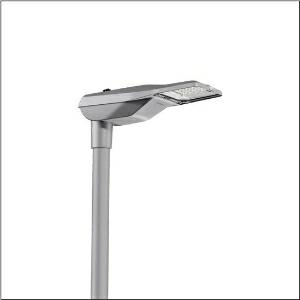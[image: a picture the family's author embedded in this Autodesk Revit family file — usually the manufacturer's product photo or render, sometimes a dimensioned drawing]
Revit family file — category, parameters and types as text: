
# Revit family: streetlight_sl_21_iq_micro___p0_8a_5xe1u31v08cb_453e
name_source: partatom
category: Lighting Fixtures
units: mm (PartAtom-declared; Revit-internal decimal feet)

## family parameters
Cut with Voids When Loaded = No
Host = Face
Light Source = No
Part Type = Normal
Room Calculation Point = No
Round Connector Dimension = Use Diameter
Shared = No

## types (1)
- --- (1 x LED, 2890 lm, 19.1 W, 3000K)
    Apparent Load = 19 VA
    CIE Flux Codes = 33 69 96 100 100
    Color Rendering = 70
    Color Temperature = 3000K
    Default Elevation = 1800 mm
    Description = Streetlight SL 21 iQ micro, mast luminaire, primary light control with lens, of PMMA, primary optical cover: cover, of toughened safety glass, transparent, light distribution: P0.8a, light emission: direct distribution, primary light characteristic: asymmetric, installation type: post-top, side-entry, LED, High Power LED, rated luminous flux: 2.890lm, luminous efficacy: 151lm/W, light colour: 730, colour temperature: 3000K, control gear: iQ-Street Remote, D4i with power reduction, control: pre-setting: logarithmic dimming characteristic, Street-Remote, Auto-Match, Temp-Guard, Lumen-Switch, Night-Set, Smart-Wire, Light-Fading, Desk-Remote (wireless, voltage-free reading and setting of iQ features in the workshop via application-optimized NFC function/RFID function), optimised constant luminous flux control (CLO 2.0), mains connection: 220..240V, AC, 50/60Hz, start of lifetime: 19W, end of service life: 20W, reduction: 9W, luminaire housing, of diecast aluminium, powder-coated, SITECO metallic grey (DB 702S), corrosivity category C5 high according to DIN EN ISO 12944, please order mast flange separately, inclination adjustable: 0°, 5°, 10°, 15°, sealing non-destructively replaceable, multi-level sealing system, length: 528mm, width: 235mm, height: 110mm, mast flange for spigot size: 42mm (side-entry): 5XC10008XM4, 60/48mm (side-entry/post-top): 5XC10108XM2, 76/60mm (side-entry/post-top): 5XC10108XM1, mounting height: 4..8m, Smart Interface above, protection rating (complete): IP66, insulation class (complete): insulation class II (safety insulation), certification: CE, ENEC, ENEC+, VDE, impact resistance: IK10, permissible operating ambient temperature for outdoor applications: -40..+50°C, standard-compliant lighting for roads and squares, packaging unit: 1 piece

Light Distribution: P0.8a
    Height = 110 mm
    Lamp = 1 x LED
    Lamp Light Flux = 2890 lm
    Lamp Power = 19.1 W
    Lamp count = 1
    Length = 528 mm
    Luminous efficacy = 151 lm/W
    Manufacturer = Siteco
    ModVariant = No
    Model = 5XE1U31V08CB
    Number of Poles = 1
    OnlyDefault = Yes
    Power Factor = 1
    Product Name = Streetlight SL 21 iQ micro | P0.8a
    Product group = mast luminaire | pylon top
    ProductGroupID = 6100
    Protection Class = Protection class II
    Protection Degree = IP 66
    RLX_Detail_Level = 1
    RLX_Emergency_Light_Flux = 0 lm
    RLX_Emergency_Type = 0
    RLX_Emergency_Type_DB = No
    RlxData = <blob elided: 98297 chars, md5=69eb93f5>
    Socket = socket
    Standby Power = 0 W
    System Light Flux = 2890 lm
    System Power = 19 W
    Type Comments = factory setting: luminous flux: 100 % | dim-lin: 254 | 387 mA
    Type Image = l_1277292.jpg
    URL = http://relux.com
    VarID = @adj_080669
    Voltage = 0 V
    Weight = 0.00 kg
    Width = 235 mm

## geometry (parser evidence)
native form markers: Blend x4, Sweep x12
no freeform markers — native parametric forms only
